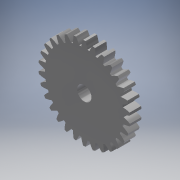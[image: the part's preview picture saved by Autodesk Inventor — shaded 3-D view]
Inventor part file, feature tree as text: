
AUTODESK INVENTOR PART (.ipt)
format: ipt  version: 2019 (Build 230136000, 136)  size: 346,624 bytes
history: native  units: mm (DEFAULTED — no unit token found)
features: other x6, plane x3, sketch x3, extrude x1, hole x1
ambient origin geometry x8: Origin, YZ Plane, XZ Plane, XY Plane, X Axis, Y Axis, Z Axis, Center Point
bodies: Solid1 (feature_tree)
feature tree (14):
  extrude  "Extrusion1"  Depth=2.0mm TaperAngle=0.0deg
  plane  "Work Plane2"
  plane  "Work Plane8"
  plane  "Work Plane9"
  other  "Przekładnia walcowa"
  hole  "Otwór1"  [1 undecoded]
  other  "Edytuj bezpośrednio1"
  sketch  "Sketch1"  dims[d0=16.0mm d1=2.0mm d2=0.0mm]
  sketch  "Sketch2"  dims[d3=15.0mm d4=10.0mm d5=0.0mm d16=10.0mm d17=0.0mm d34=1.047198mm d39=0.0mm d41=0.0mm d43=10.0mm d46=10.0mm d47=0.0mm d48=0.0mm d49=2.5mm d50=6.0mm d51=4.0mm d52=2.0mm d53=90.0deg d54=8.0mm d55=20.594885mm d56=0.0mm d57=0.0mm d58=-0.3mm d59=0.0mm d60=0.0mm d61=0.3mm]
  other  "Srf1"
  sketch  "Szkic3"
  other  "Średnica podziałowa"
  other  "Przesuń1"
  other  "Przesuń2"
note: 1 required parameter value undecoded (feature->parameter linkage not recoverable at this tier; creation-order binding heuristic only, values carry confidence <= 0.55)
